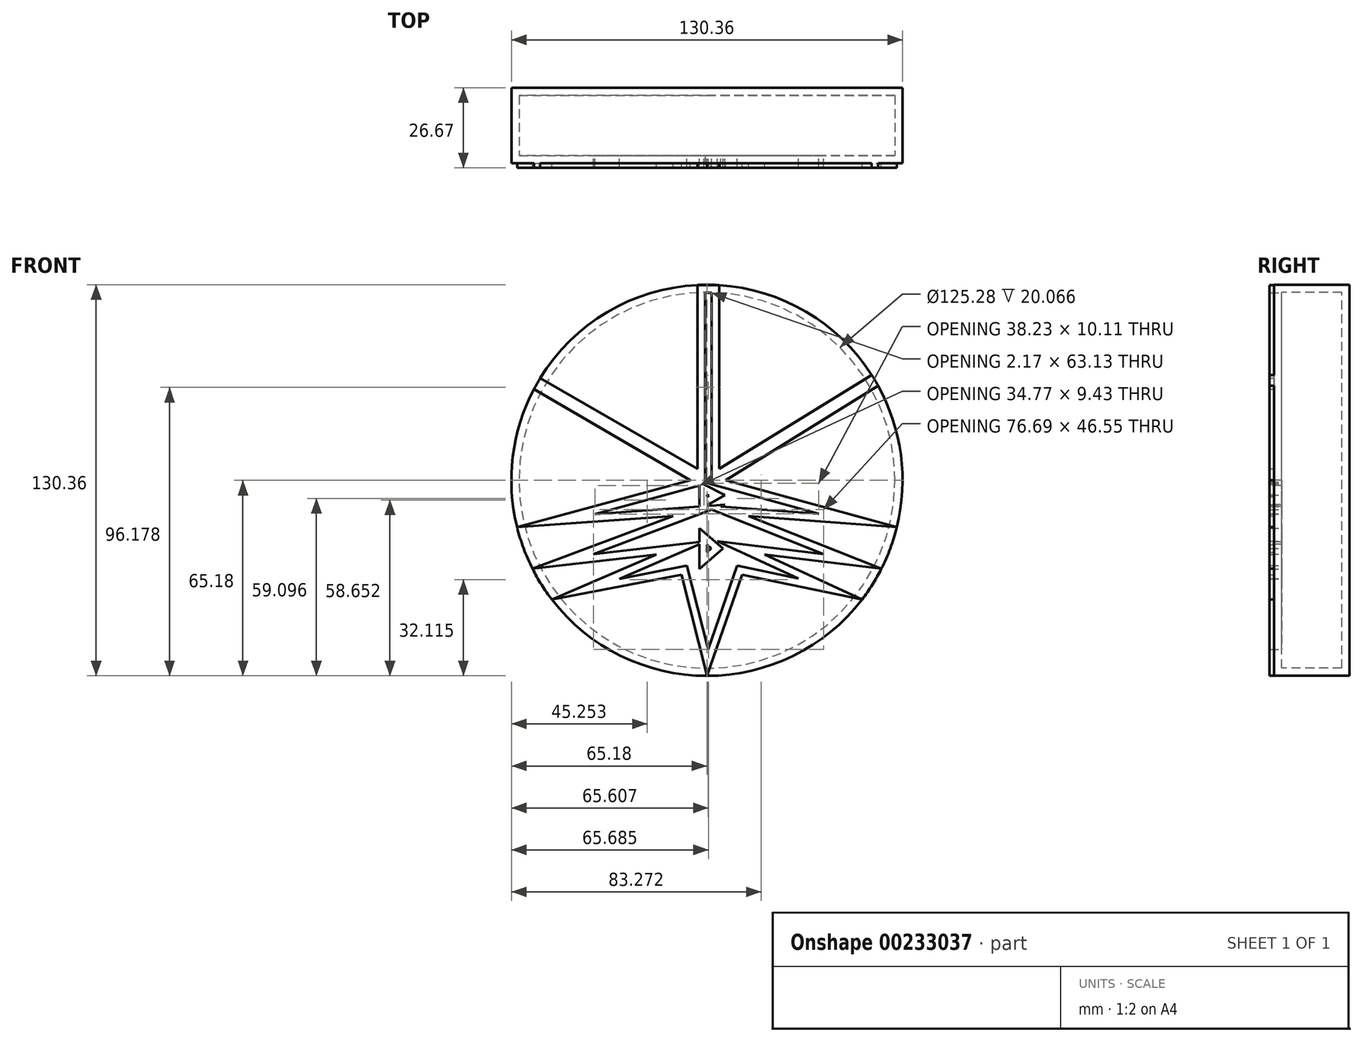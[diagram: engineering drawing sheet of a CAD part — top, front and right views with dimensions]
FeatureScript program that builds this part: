
annotation { "Feature Type Name" : "Feature", "Feature Type Description" : "" }
export const myFeature = defineFeature(function(context is Context, id is Id, definition is map)
    precondition{}
    {
        {
            var Q0;
            Q0=qCreatedBy(makeId("Front.planeOp"),FACE);
            var sketch = newSketch(context, id + "F0", { "sketchPlane" : qUnion([Q0])});
            skCircle(sketch, "E0", {"center": v(0, 0) * mm, "radius": 65.18 * mm});
            skSolve(sketch);
        }
        {
            var Q0;
            Q0=makeQuery(id+"F0.imprint","IMPRINT",FACE,{"disambiguationData":[TD([[makeQuery(id+"F0.imprint","IMPRINT",EDGE,{"derivedFrom":sQuery(id+"F0.wireOp",EDGE,"E0")}),1.0]])]});
            extrude(context, id + "F1", {"entities" : qUnion([Q0]), "oppositeDirection" : true, "depth" : 25.15 * mm});
        }
        {
            var Q0;
            Q0=makeQuery(id+"F1.opExtrude","CAP_FACE",FACE,{"disambiguationData":[OSD([sQuery(id+"F0.wireOp",EDGE,"E0")])],"isStart":true});
            var sketch = newSketch(context, id + "F2", { "sketchPlane" : qUnion([Q0])});
            skLineSegment(sketch, "E1", {"start": v(-57.66, 30.4) * mm, "end": v(-5.56, 0) * mm});
            skLineSegment(sketch, "E2", {"start": v(-55.6, 34) * mm, "end": v(-3.2, 3.84) * mm});
            skLineSegment(sketch, "E3", {"start": v(-3.2, 3.84) * mm, "end": v(-3.2, 65.1) * mm});
            skLineSegment(sketch, "E4", {"start": v(-3.2, 65.1) * mm, "end": v(0, 65.1) * mm});
            skLineSegment(sketch, "E5", {"start": v(0, 65.1) * mm, "end": v(0, 3.84) * mm});
            skLineSegment(sketch, "E6", {"start": v(11.74, -31.42) * mm, "end": v(51.66, -39.75) * mm});
            skLineSegment(sketch, "E7", {"start": v(51.66, -39.75) * mm, "end": v(19.2, -24.73) * mm});
            skLineSegment(sketch, "E8", {"start": v(19.2, -24.73) * mm, "end": v(58.13, -29.5) * mm});
            skLineSegment(sketch, "E9", {"start": v(58.13, -29.5) * mm, "end": v(13.87, -11.92) * mm});
            skLineSegment(sketch, "E10", {"start": v(13.87, -11.92) * mm, "end": v(63.27, -15.65) * mm});
            skLineSegment(sketch, "E11", {"start": v(63.27, -15.65) * mm, "end": v(6.19, 0) * mm});
            skLineSegment(sketch, "E12", {"start": v(6.19, 0) * mm, "end": v(57.05, 31.53) * mm});
            skLineSegment(sketch, "E13", {"start": v(54.95, 35.06) * mm, "end": v(4.05, 3.84) * mm});
            skLineSegment(sketch, "E14", {"start": v(4.05, 3.84) * mm, "end": v(4.05, 65.05) * mm});
            skLineSegment(sketch, "E15", {"start": v(4.05, 65.05) * mm, "end": v(0, 65.1) * mm});
            skLineSegment(sketch, "E16", {"start": v(-5.56, 0) * mm, "end": v(-63.27, -15.65) * mm});
            skLineSegment(sketch, "E17", {"start": v(-63.27, -15.65) * mm, "end": v(-11.3, -11.92) * mm});
            skLineSegment(sketch, "E18", {"start": v(-11.3, -11.92) * mm, "end": v(-58.13, -29.5) * mm});
            skLineSegment(sketch, "E19", {"start": v(-58.13, -29.5) * mm, "end": v(-16.86, -24.73) * mm});
            skLineSegment(sketch, "E20", {"start": v(-16.86, -24.73) * mm, "end": v(-51.66, -39.75) * mm});
            skLineSegment(sketch, "E21", {"start": v(-51.66, -39.75) * mm, "end": v(-8.53, -31.42) * mm});
            skLineSegment(sketch, "E22", {"start": v(-8.53, -31.42) * mm, "end": v(0, -65.18) * mm});
            skLineSegment(sketch, "E23", {"start": v(0, -65.18) * mm, "end": v(11.74, -31.42) * mm});
            skLineSegment(sketch, "E24", {"start": v(-3.2, 3.84) * mm, "end": v(-5.56, 0) * mm});
            skLineSegment(sketch, "E25", {"start": v(0, 3.84) * mm, "end": v(-3.2, 3.84) * mm});
            skLineSegment(sketch, "E26", {"start": v(0, 3.84) * mm, "end": v(4.05, 3.84) * mm});
            skLineSegment(sketch, "E27", {"start": v(6.19, 0) * mm, "end": v(4.05, 3.84) * mm});
            skLineSegment(sketch, "E28", {"start": v(6.19, -1.92) * mm, "end": v(13.87, -11.92) * mm});
            skLineSegment(sketch, "E29", {"start": v(6.19, -1.92) * mm, "end": v(6.19, 0) * mm});
            skLineSegment(sketch, "E30", {"start": v(-5.56, -1.92) * mm, "end": v(-11.3, -11.92) * mm});
            skLineSegment(sketch, "E31", {"start": v(-5.56, -1.92) * mm, "end": v(-5.56, 0) * mm});
            skLineSegment(sketch, "E32", {"start": v(0, 3.84) * mm, "end": v(0, -65.18) * mm});
            skLineSegment(sketch, "E33", {"start": v(-8.53, -31.42) * mm, "end": v(13.87, -11.92) * mm});
            skLineSegment(sketch, "E34", {"start": v(-11.3, -11.92) * mm, "end": v(11.74, -31.42) * mm});
            skLineSegment(sketch, "E35", {"start": v(-11.3, -11.92) * mm, "end": v(-16.86, -24.73) * mm});
            skLineSegment(sketch, "E36", {"start": v(-8.53, -31.42) * mm, "end": v(-16.86, -24.73) * mm});
            skLineSegment(sketch, "E37", {"start": v(13.87, -11.92) * mm, "end": v(19.2, -24.73) * mm});
            skLineSegment(sketch, "E38", {"start": v(11.74, -31.42) * mm, "end": v(19.2, -24.73) * mm});
            skLineSegment(sketch, "E39", {"start": v(-5.56, -1.92) * mm, "end": v(13.87, -11.92) * mm});
            skLineSegment(sketch, "E40", {"start": v(6.19, -1.92) * mm, "end": v(-11.3, -11.92) * mm});
            skLineSegment(sketch, "E41", {"start": v(-5.56, 0) * mm, "end": v(6.19, 0) * mm});
            skLineSegment(sketch, "E42", {"start": v(-3.2, 3.84) * mm, "end": v(0, 0) * mm});
            skLineSegment(sketch, "E43", {"start": v(0, 0) * mm, "end": v(4.05, 3.84) * mm});
            skLineSegment(sketch, "E44", {"start": v(0, 3.84) * mm, "end": v(0, 0) * mm});
            skSolve(sketch);
        }
        {
            var Q0;
            {var subQ0=sQuery(id+"F2.wireOp",EDGE,"E1");Q0=makeQuery(id+"F2.imprint","IMPRINT",FACE,{"disambiguationData":[TD([[makeQuery(id+"F2.imprint","IMPRINT",EDGE,{"derivedFrom":subQ0}),1.0]])]});}
            var Q1;
            Q1=makeQuery(id+"F2.imprint","IMPRINT",FACE,{"disambiguationData":[TD([[makeQuery(id+"F2.imprint","IMPRINT",EDGE,{"derivedFrom":sQuery(id+"F2.wireOp",EDGE,"E5")}),1.0]])]});
            var Q2;
            Q2=makeQuery(id+"F2.imprint","IMPRINT",FACE,{"disambiguationData":[TD([[makeQuery(id+"F2.imprint","IMPRINT",EDGE,{"derivedFrom":sQuery(id+"F2.wireOp",EDGE,"E3")}),-1.0]])]});
            var Q3;
            {var subQ0=sQuery(id+"F2.wireOp",EDGE,"E12");Q3=makeQuery(id+"F2.imprint","IMPRINT",FACE,{"disambiguationData":[TD([[makeQuery(id+"F2.imprint","IMPRINT",EDGE,{"derivedFrom":subQ0}),1.0]])]});}
            var Q4;
            {var subQ0=sQuery(id+"F2.wireOp",EDGE,"E27");Q4=makeQuery(id+"F2.imprint","IMPRINT",FACE,{"disambiguationData":[TD([[makeQuery(id+"F2.imprint","IMPRINT",EDGE,{"derivedFrom":subQ0}),1.0]])]});}
            var Q5;
            Q5=makeQuery(id+"F2.imprint","IMPRINT",FACE,{"disambiguationData":[TD([[makeQuery(id+"F2.imprint","IMPRINT",EDGE,{"derivedFrom":sQuery(id+"F2.wireOp",EDGE,"E26")}),-1.0]])]});
            var Q6;
            Q6=makeQuery(id+"F2.imprint","IMPRINT",FACE,{"disambiguationData":[TD([[makeQuery(id+"F2.imprint","IMPRINT",EDGE,{"derivedFrom":sQuery(id+"F2.wireOp",EDGE,"E25")}),1.0]])]});
            var Q7;
            {var subQ0=sQuery(id+"F2.wireOp",EDGE,"E24");Q7=makeQuery(id+"F2.imprint","IMPRINT",FACE,{"disambiguationData":[TD([[makeQuery(id+"F2.imprint","IMPRINT",EDGE,{"derivedFrom":subQ0}),1.0]])]});}
            var Q8;
            {var subQ0=sQuery(id+"F2.wireOp",EDGE,"E31");Q8=makeQuery(id+"F2.imprint","IMPRINT",FACE,{"disambiguationData":[TD([[makeQuery(id+"F2.imprint","IMPRINT",EDGE,{"derivedFrom":subQ0}),-1.0]])]});}
            var Q9;
            {var subQ1=sQuery(id+"F2.wireOp",EDGE,"E29");Q9=makeQuery(id+"F2.imprint","IMPRINT",FACE,{"disambiguationData":[TD([[makeQuery(id+"F2.imprint","IMPRINT",EDGE,{"derivedFrom":subQ1}),1.0]])]});}
            var Q10;
            {var subQ0=sQuery(id+"F2.wireOp",EDGE,"E30");Q10=makeQuery(id+"F2.imprint","IMPRINT",FACE,{"disambiguationData":[TD([[makeQuery(id+"F2.imprint","IMPRINT",EDGE,{"derivedFrom":subQ0}),1.0]])]});}
            var Q11;
            {var subQ0=sQuery(id+"F2.wireOp",EDGE,"E28");Q11=makeQuery(id+"F2.imprint","IMPRINT",FACE,{"disambiguationData":[TD([[makeQuery(id+"F2.imprint","IMPRINT",EDGE,{"derivedFrom":subQ0}),-1.0]])]});}
            var Q12;
            {var subQ5=sQuery(id+"F2.wireOp",EDGE,"E40");var subQ6=sQuery(id+"F2.wireOp",EDGE,"E32");var subQ7=makeQuery(id+"F2.imprint","INTERSECT",VERTEX,{"derivedFrom":[subQ6,subQ5]});Q12=makeQuery(id+"F2.imprint","IMPRINT",FACE,{"disambiguationData":[TD([[makeQuery(id+"F2.imprint","IMPRINT",EDGE,{"disambiguationData":[TD([[subQ7,-1.0]])],"derivedFrom":subQ6}),1.0]])]});}
            var Q13;
            {var subQ0=sQuery(id+"F2.wireOp",EDGE,"E40");var subQ1=sQuery(id+"F2.wireOp",EDGE,"E32");var subQ2=makeQuery(id+"F2.imprint","INTERSECT",VERTEX,{"derivedFrom":[subQ1,subQ0]});Q13=makeQuery(id+"F2.imprint","IMPRINT",FACE,{"disambiguationData":[TD([[makeQuery(id+"F2.imprint","IMPRINT",EDGE,{"disambiguationData":[TD([[subQ2,-1.0]])],"derivedFrom":subQ1}),-1.0]])]});}
            var Q14;
            Q14=makeQuery(id+"F2.imprint","IMPRINT",FACE,{"disambiguationData":[TD([[makeQuery(id+"F2.imprint","IMPRINT",EDGE,{"derivedFrom":sQuery(id+"F2.wireOp",EDGE,"E16")}),1.0]])]});
            var Q15;
            Q15=makeQuery(id+"F2.imprint","IMPRINT",FACE,{"disambiguationData":[TD([[makeQuery(id+"F2.imprint","IMPRINT",EDGE,{"derivedFrom":sQuery(id+"F2.wireOp",EDGE,"E18")}),1.0]])]});
            var Q16;
            Q16=makeQuery(id+"F2.imprint","IMPRINT",FACE,{"disambiguationData":[TD([[makeQuery(id+"F2.imprint","IMPRINT",EDGE,{"derivedFrom":sQuery(id+"F2.wireOp",EDGE,"E20")}),1.0]])]});
            var Q17;
            {var subQ0=sQuery(id+"F2.wireOp",EDGE,"E35");Q17=makeQuery(id+"F2.imprint","IMPRINT",FACE,{"disambiguationData":[TD([[makeQuery(id+"F2.imprint","IMPRINT",EDGE,{"derivedFrom":subQ0}),1.0]])]});}
            var Q18;
            {var subQ0=sQuery(id+"F2.wireOp",EDGE,"E23");Q18=makeQuery(id+"F2.imprint","IMPRINT",FACE,{"disambiguationData":[TD([[makeQuery(id+"F2.imprint","IMPRINT",EDGE,{"derivedFrom":subQ0}),1.0]])]});}
            var Q19;
            {var subQ0=sQuery(id+"F2.wireOp",EDGE,"E22");Q19=makeQuery(id+"F2.imprint","IMPRINT",FACE,{"disambiguationData":[TD([[makeQuery(id+"F2.imprint","IMPRINT",EDGE,{"derivedFrom":subQ0}),1.0]])]});}
            var Q20;
            {var subQ0=sQuery(id+"F2.wireOp",EDGE,"E37");Q20=makeQuery(id+"F2.imprint","IMPRINT",FACE,{"disambiguationData":[TD([[makeQuery(id+"F2.imprint","IMPRINT",EDGE,{"derivedFrom":subQ0}),-1.0]])]});}
            var Q21;
            Q21=makeQuery(id+"F2.imprint","IMPRINT",FACE,{"disambiguationData":[TD([[makeQuery(id+"F2.imprint","IMPRINT",EDGE,{"derivedFrom":sQuery(id+"F2.wireOp",EDGE,"E6")}),1.0]])]});
            var Q22;
            Q22=makeQuery(id+"F2.imprint","IMPRINT",FACE,{"disambiguationData":[TD([[makeQuery(id+"F2.imprint","IMPRINT",EDGE,{"derivedFrom":sQuery(id+"F2.wireOp",EDGE,"E8")}),1.0]])]});
            var Q23;
            Q23=makeQuery(id+"F2.imprint","IMPRINT",FACE,{"disambiguationData":[TD([[makeQuery(id+"F2.imprint","IMPRINT",EDGE,{"derivedFrom":sQuery(id+"F2.wireOp",EDGE,"E10")}),1.0]])]});
            extrude(context, id + "F3", {"entities" : qUnion([Q0, Q1, Q2, Q3, Q4, Q5, Q6, Q7, Q8, Q9, Q10, Q11, Q12, Q13, Q14, Q15, Q16, Q17, Q18, Q19, Q20, Q21, Q22, Q23]), "operationType" : NewBodyOperationType.ADD, "depth" : 1.52 * mm});
        }
        {
            var Q0;
            Q0=makeQuery(id+"F3.opExtrude","CAP_FACE",FACE,{"disambiguationData":[OSD([sQuery(id+"F0.wireOp",EDGE,"E0"),sQuery(id+"F2.wireOp",EDGE,"E1"),sQuery(id+"F2.wireOp",EDGE,"E2"),sQuery(id+"F2.wireOp",EDGE,"E3"),sQuery(id+"F2.wireOp",EDGE,"E4"),sQuery(id+"F2.wireOp",EDGE,"E6"),sQuery(id+"F2.wireOp",EDGE,"E7"),sQuery(id+"F2.wireOp",EDGE,"E8"),sQuery(id+"F2.wireOp",EDGE,"E9"),sQuery(id+"F2.wireOp",EDGE,"E10"),sQuery(id+"F2.wireOp",EDGE,"E11"),sQuery(id+"F2.wireOp",EDGE,"E12"),sQuery(id+"F2.wireOp",EDGE,"E13"),sQuery(id+"F2.wireOp",EDGE,"E14"),sQuery(id+"F2.wireOp",EDGE,"E15"),sQuery(id+"F2.wireOp",EDGE,"E16"),sQuery(id+"F2.wireOp",EDGE,"E17"),sQuery(id+"F2.wireOp",EDGE,"E18"),sQuery(id+"F2.wireOp",EDGE,"E19"),sQuery(id+"F2.wireOp",EDGE,"E20"),sQuery(id+"F2.wireOp",EDGE,"E21"),sQuery(id+"F2.wireOp",EDGE,"E22"),sQuery(id+"F2.wireOp",EDGE,"E23"),sQuery(id+"F2.wireOp",EDGE,"E32"),sQuery(id+"F2.wireOp",EDGE,"E33"),sQuery(id+"F2.wireOp",EDGE,"E34"),sQuery(id+"F2.wireOp",EDGE,"E39"),sQuery(id+"F2.wireOp",EDGE,"E40")])],"isStart":false});
            shell(context, id + "F4", {"entities" : qUnion([Q0]), "thickness" : 2.54 * mm});
        }
    });
